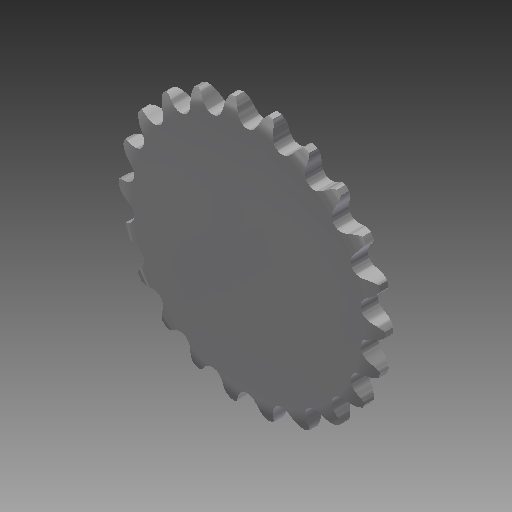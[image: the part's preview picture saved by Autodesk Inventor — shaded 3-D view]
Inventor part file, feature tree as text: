
AUTODESK INVENTOR PART (.ipt)
format: ipt  version: 2017 (Build 210142000, 142)  size: 616,960 bytes
history: native  units: mm
features: other x6, extrude x2, pattern_linear x1, pattern_circular x1
ambient origin geometry x8: Origin, YZ Plane, XZ Plane, XY Plane, X Axis, Y Axis, Z Axis, Center Point
bodies: Solid1 (feature_tree)
feature tree (10):
  other  "Theoretical Tooth Profile"
  other  "Tooth Profile"
  other  "Section Profile"
  other  "Shroud"
  other  "Strand"
  pattern_linear  "Strand Pattern"  Spacing1=44.619381mm  [1 undecoded]
  extrude  "Theoretical Tooth"  Depth=2.855993mm
  extrude  "Tooth"  Depth=1.697355mm
  pattern_circular  "Tooth Pattern"  [2 undecoded]
  other  "Timing Plane"
note: 3 required parameter values undecoded (feature->parameter linkage not recoverable at this tier; creation-order binding heuristic only, values carry confidence <= 0.55)
